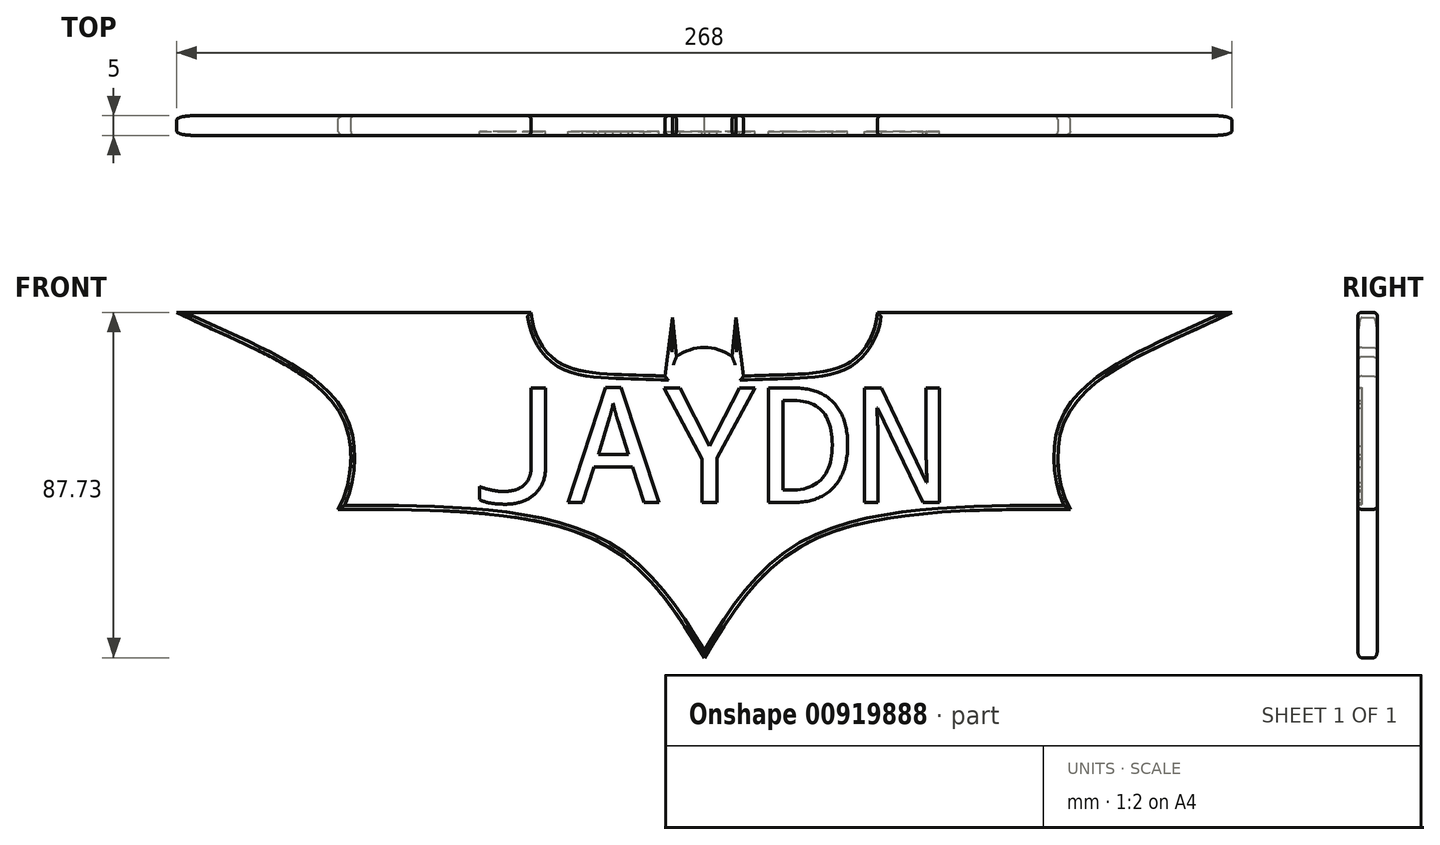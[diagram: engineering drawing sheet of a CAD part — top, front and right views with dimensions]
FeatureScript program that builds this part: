
annotation { "Feature Type Name" : "Feature", "Feature Type Description" : "" }
export const myFeature = defineFeature(function(context is Context, id is Id, definition is map)
    precondition{}
    {
        {
            var Q0;
            Q0=qCreatedBy(makeId("Front.planeOp"),FACE);
            var sketch = newSketch(context, id + "F0", { "sketchPlane" : qUnion([Q0])});
            skArc(sketch, "E0", {"start": v(7.06, 43.8) * mm, "mid": v(0, 46.17) * mm, "end": v(-7.06, 43.8) * mm});
            skLineSegment(sketch, "E1", {"start": v(-7.06, 43.8) * mm, "end": v(-8.09, 53.75) * mm});
            skLineSegment(sketch, "E2", {"start": v(-8.09, 53.75) * mm, "end": v(-10, 38.88) * mm});
            skFitSpline(sketch, "E3", {"points": [v(-10, 38.88) * mm, v(-36.7, 42.22) * mm, v(-44, 55.04) * mm], "startDerivative": vector(-67.87, 3.06) * mm, "endDerivative": vector(-3.47, 40.54) * mm});
            skLineSegment(sketch, "E4", {"start": v(-44, 55.04) * mm, "end": v(-134, 55.04) * mm});
            skFitSpline(sketch, "E5", {"points": [v(-134, 55.04) * mm, v(-92.16, 28.77) * mm, v(-93, 5.04) * mm], "startDerivative": vector(83.7, -40.96) * mm, "endDerivative": vector(-21.5, -36.05) * mm});
            skFitSpline(sketch, "E6", {"points": [v(-93, 5.04) * mm, v(-26.28, -3.43) * mm, v(0, -32.69) * mm], "startDerivative": vector(133.91, -0.06) * mm, "endDerivative": vector(48.28, -78.9) * mm});
            skFitSpline(sketch, "E7.MirrorCS", {"points": [v(93, 5.04) * mm, v(26.28, -3.43) * mm, v(0, -32.69) * mm], "startDerivative": vector(-133.91, -0.06) * mm, "endDerivative": vector(-48.28, -78.9) * mm});
            skFitSpline(sketch, "E8.MirrorCS", {"points": [v(134, 55.04) * mm, v(92.16, 28.77) * mm, v(93, 5.04) * mm], "startDerivative": vector(-83.7, -40.96) * mm, "endDerivative": vector(21.5, -36.05) * mm});
            skLineSegment(sketch, "E9.MirrorCS", {"start": v(44, 55.04) * mm, "end": v(134, 55.04) * mm});
            skFitSpline(sketch, "E10.MirrorCS", {"points": [v(10, 38.88) * mm, v(36.7, 42.22) * mm, v(44, 55.04) * mm], "startDerivative": vector(67.87, 3.06) * mm, "endDerivative": vector(3.47, 40.54) * mm});
            skLineSegment(sketch, "E11.MirrorCS", {"start": v(7.06, 43.8) * mm, "end": v(8.09, 53.75) * mm});
            skLineSegment(sketch, "E12.MirrorCS", {"start": v(8.09, 53.75) * mm, "end": v(10, 38.88) * mm});
            skSolve(sketch);
        }
        {
            var Q0;
            Q0=makeQuery(id+"F0.imprint","IMPRINT",FACE,{"disambiguationData":[TD([[makeQuery(id+"F0.imprint","IMPRINT",EDGE,{"derivedFrom":sQuery(id+"F0.wireOp",EDGE,"E0")}),1.0]])]});
            extrude(context, id + "F1", {"entities" : qUnion([Q0]), "depth" : 5 * mm});
        }
        {
            var Q0;
            Q0=qCreatedBy(makeId("Front.planeOp"),FACE);
            var sketch = newSketch(context, id + "F2", { "sketchPlane" : qUnion([Q0])});
            skText(sketch, "E13", { "text": "JAYDN", "fontName": "DroidSansMono.ttf"});
            const initialGuessF2  = {"E13": [-0.0598, 0.00673, 1, 0, 0.02935]};
            skSetInitialGuess(sketch, initialGuessF2);
            skSolve(sketch);
        }
        {
            var Q0;
            Q0=qSketchRegion(id+"F2",true);
            extrude(context, id + "F3", {"entities" : qUnion([Q0]), "operationType" : NewBodyOperationType.REMOVE, "depth" : 5 * mm, "hasSecondDirection" : true, "secondDirectionOppositeDirection" : false, "secondDirectionDepth" : 4 * mm});
        }
        {
            var Q0;
            Q0=makeQuery(id+"F1.opExtrude","CAP_EDGE",EDGE,{"disambiguationData":[OSD([sQuery(id+"F0.wireOp",EDGE,"E4")])],"isStart":false});
            var Q1;
            Q1=makeQuery(id+"F1.opExtrude","CAP_EDGE",EDGE,{"disambiguationData":[OSD([sQuery(id+"F0.wireOp",EDGE,"E5")])],"isStart":false});
            var Q2;
            Q2=makeQuery(id+"F1.opExtrude","CAP_EDGE",EDGE,{"disambiguationData":[OSD([sQuery(id+"F0.wireOp",EDGE,"E6")])],"isStart":false});
            var Q3;
            Q3=makeQuery(id+"F1.opExtrude","CAP_EDGE",EDGE,{"disambiguationData":[OSD([sQuery(id+"F0.wireOp",EDGE,"E7.MirrorCS")])],"isStart":false});
            var Q4;
            Q4=makeQuery(id+"F1.opExtrude","CAP_EDGE",EDGE,{"disambiguationData":[OSD([sQuery(id+"F0.wireOp",EDGE,"E8.MirrorCS")])],"isStart":false});
            var Q5;
            Q5=makeQuery(id+"F1.opExtrude","CAP_EDGE",EDGE,{"disambiguationData":[OSD([sQuery(id+"F0.wireOp",EDGE,"E9.MirrorCS")])],"isStart":false});
            var Q6;
            Q6=makeQuery(id+"F1.opExtrude","CAP_EDGE",EDGE,{"disambiguationData":[OSD([sQuery(id+"F0.wireOp",EDGE,"E11.MirrorCS")])],"isStart":false});
            var Q7;
            Q7=makeQuery(id+"F1.opExtrude","CAP_EDGE",EDGE,{"disambiguationData":[OSD([sQuery(id+"F0.wireOp",EDGE,"E1")])],"isStart":false});
            var Q8;
            Q8=makeQuery(id+"F1.opExtrude","CAP_EDGE",EDGE,{"disambiguationData":[OSD([sQuery(id+"F0.wireOp",EDGE,"E0")])],"isStart":false});
            var Q9;
            Q9=makeQuery(id+"F1.opExtrude","CAP_EDGE",EDGE,{"disambiguationData":[OSD([sQuery(id+"F0.wireOp",EDGE,"E2")])],"isStart":false});
            var Q10;
            Q10=makeQuery(id+"F1.opExtrude","CAP_EDGE",EDGE,{"disambiguationData":[OSD([sQuery(id+"F0.wireOp",EDGE,"E12.MirrorCS")])],"isStart":false});
            var Q11;
            Q11=makeQuery(id+"F1.opExtrude","CAP_EDGE",EDGE,{"disambiguationData":[OSD([sQuery(id+"F0.wireOp",EDGE,"E10.MirrorCS")])],"isStart":false});
            var Q12;
            Q12=makeQuery(id+"F1.opExtrude","CAP_EDGE",EDGE,{"disambiguationData":[OSD([sQuery(id+"F0.wireOp",EDGE,"E3")])],"isStart":false});
            var Q13;
            Q13=makeQuery(id+"F1.opExtrude","CAP_EDGE",EDGE,{"disambiguationData":[OSD([sQuery(id+"F0.wireOp",EDGE,"E12.MirrorCS")])],"isStart":true});
            var Q14;
            Q14=makeQuery(id+"F1.opExtrude","CAP_EDGE",EDGE,{"disambiguationData":[OSD([sQuery(id+"F0.wireOp",EDGE,"E11.MirrorCS")])],"isStart":true});
            var Q15;
            Q15=makeQuery(id+"F1.opExtrude","CAP_EDGE",EDGE,{"disambiguationData":[OSD([sQuery(id+"F0.wireOp",EDGE,"E0")])],"isStart":true});
            var Q16;
            Q16=makeQuery(id+"F1.opExtrude","CAP_EDGE",EDGE,{"disambiguationData":[OSD([sQuery(id+"F0.wireOp",EDGE,"E1")])],"isStart":true});
            var Q17;
            Q17=makeQuery(id+"F1.opExtrude","CAP_EDGE",EDGE,{"disambiguationData":[OSD([sQuery(id+"F0.wireOp",EDGE,"E2")])],"isStart":true});
            var Q18;
            Q18=makeQuery(id+"F1.opExtrude","CAP_EDGE",EDGE,{"disambiguationData":[OSD([sQuery(id+"F0.wireOp",EDGE,"E3")])],"isStart":true});
            var Q19;
            Q19=makeQuery(id+"F1.opExtrude","CAP_EDGE",EDGE,{"disambiguationData":[OSD([sQuery(id+"F0.wireOp",EDGE,"E10.MirrorCS")])],"isStart":true});
            var Q20;
            Q20=makeQuery(id+"F1.opExtrude","CAP_EDGE",EDGE,{"disambiguationData":[OSD([sQuery(id+"F0.wireOp",EDGE,"E9.MirrorCS")])],"isStart":true});
            var Q21;
            Q21=makeQuery(id+"F1.opExtrude","CAP_EDGE",EDGE,{"disambiguationData":[OSD([sQuery(id+"F0.wireOp",EDGE,"E8.MirrorCS")])],"isStart":true});
            var Q22;
            Q22=makeQuery(id+"F1.opExtrude","CAP_EDGE",EDGE,{"disambiguationData":[OSD([sQuery(id+"F0.wireOp",EDGE,"E7.MirrorCS")])],"isStart":true});
            var Q23;
            Q23=makeQuery(id+"F1.opExtrude","CAP_EDGE",EDGE,{"disambiguationData":[OSD([sQuery(id+"F0.wireOp",EDGE,"E6")])],"isStart":true});
            var Q24;
            Q24=makeQuery(id+"F1.opExtrude","CAP_EDGE",EDGE,{"disambiguationData":[OSD([sQuery(id+"F0.wireOp",EDGE,"E5")])],"isStart":true});
            var Q25;
            Q25=makeQuery(id+"F1.opExtrude","CAP_EDGE",EDGE,{"disambiguationData":[OSD([sQuery(id+"F0.wireOp",EDGE,"E4")])],"isStart":true});
            fillet(context, id + "F4", {"entities" : qUnion([Q0, Q1, Q2, Q3, Q4, Q5, Q6, Q7, Q8, Q9, Q10, Q11, Q12, Q13, Q14, Q15, Q16, Q17, Q18, Q19, Q20, Q21, Q22, Q23, Q24, Q25]), "radius" : 1 * mm, "tangentPropagation" : true, "allowEdgeOverflow" : false});
        }
    });
